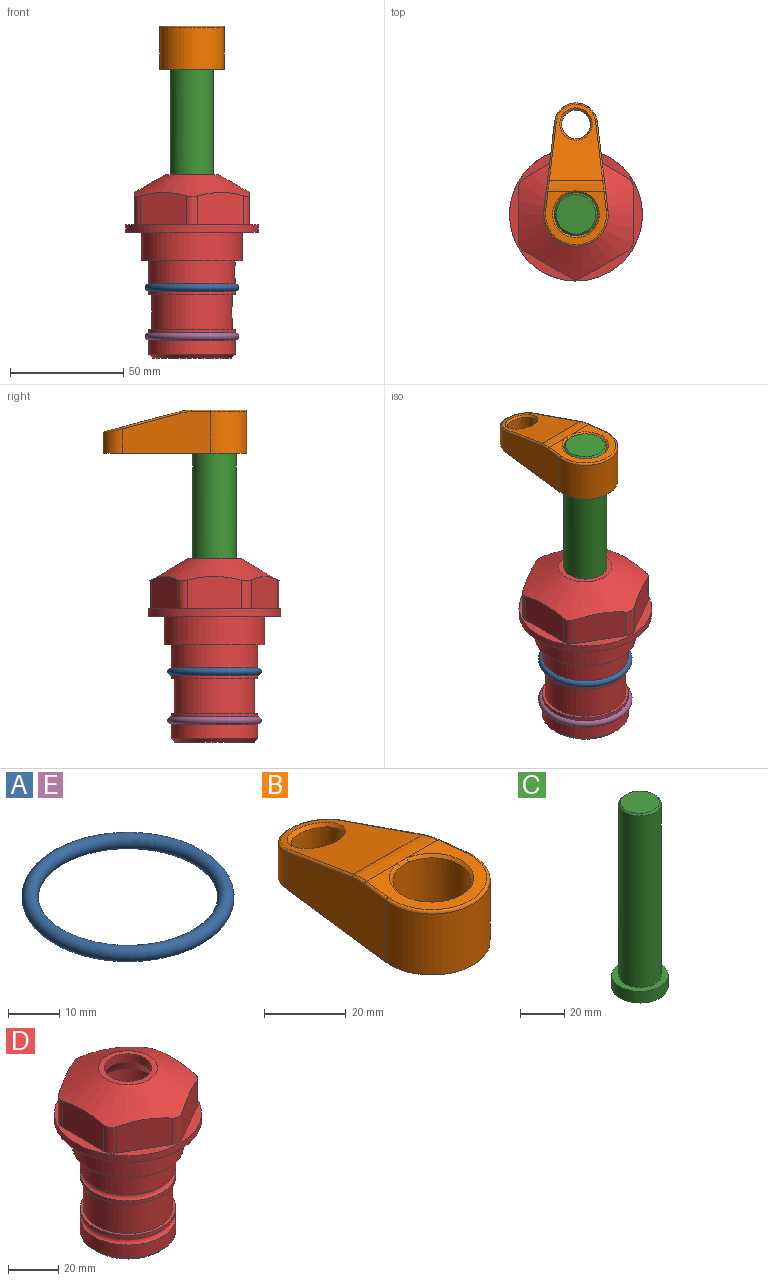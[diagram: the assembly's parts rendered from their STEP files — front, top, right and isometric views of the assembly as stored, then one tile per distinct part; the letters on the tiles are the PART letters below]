
ASSEMBLY  parts=5 mates=4
PART A: 1 faces, bbox 44.7x44.7x3.2 mm
  f0: torus R=19.05mm, axis (0,0,1), area 1193.9mm2
PART B: 31 faces, bbox 31.7x65.5x19.8 mm
  f0: plane 39.12x18.26mm, normal (0.99,0.12,0), area 612.2mm2, adj f1,f4,f7,f11,f13,f15
  f1: cylinder r=9.53mm len=18.91mm, axis (0,0,-1), area 296.1mm2, adj f0,f2,f7,f17
  f2: plane 39.12x18.26mm, normal (-0.99,0.12,0), area 612.2mm2, adj f1,f4,f7,f12,f14,f16
  f3: cylinder r=6.35mm len=12.7mm, axis (0,0,-1), area 362.4mm2, adj f7,f18
  f4: cylinder r=14.29mm len=28.58mm, axis (0,0,-1), area 882.2mm2, adj f0,f2,f7,f10
  f5: cylinder r=9.53mm len=19.05mm, axis (0,0,-1), area 1092.6mm2, adj f7,f19,f20
  f6: plane 26.99x23.69mm, normal (0,0,1), area 216.2mm2, adj f9,f10,f11,f12,f19
  f7: plane 63.5x28.58mm, normal (0,0,-1), area 661.8mm2, adj f0,f1,f2,f3,f4,f5,f22,f23
  f8: plane 33.52x23.6mm, normal (0,0.26,0.97), area 486mm2, adj f9,f15,f16,f17,f18
  f9: cylinder r=19.05mm len=24.72mm, axis (1,0,0), area 120.4mm2, adj f6,f8,f13,f14,f20
  f10: torus R=13.49mm, axis (0,0,1), area 59mm2, adj f4,f6,f11,f12
  f11: cylinder r=0.79mm len=8.67mm, axis (0.12,-0.99,0), area 10.8mm2, adj f0,f6,f10,f13
  f12: cylinder r=0.79mm len=8.67mm, axis (0.12,0.99,0), area 10.8mm2, adj f2,f6,f10,f14
  f13: bspline ~4.95x1.42mm, area 6.1mm2, adj f0,f9,f11,f15
  f14: bspline ~4.95x1.42mm, area 6.1mm2, adj f2,f9,f12,f16
  f15: cylinder r=0.79mm len=25.95mm, axis (0.12,-0.96,0.26), area 32.9mm2, adj f0,f8,f13,f17
  f16: cylinder r=0.79mm len=25.95mm, axis (0.12,0.96,-0.26), area 32.9mm2, adj f2,f8,f14,f17
  f17: bspline ~18.91x8.38mm, area 30mm2, adj f1,f8,f15,f16
  f18: bspline ~14.29x14.29mm, area 48.3mm2, adj f3,f8
  f19: cone r=9.53mm half-angle=45deg, axis (0,0,1), area 66.5mm2, adj f5,f6,f20
  f20: bspline ~3.22x0.96mm, area 3.5mm2, adj f5,f9,f19
  f21: plane 2.75x2.72mm, normal (0,0,-1), area 2.9mm2, adj f23,f25,f28
  f22: plane 23.05x15.88mm, normal (-0.99,-0.12,0), area 323.6mm2, adj f7,f25,f26,f27,f28,f29
  f23: plane 23.05x15.88mm, normal (0.99,-0.12,0), area 323.6mm2, adj f7,f21,f25,f27,f28,f30
  f24: cylinder r=9.53mm len=10.69mm, axis (0,0,-1), area 114.7mm2, adj f7,f27,f29,f30
  f25: cylinder r=12.7mm len=20.59mm, axis (0,0,-1), area 381.1mm2, adj f7,f21,f22,f23,f26,f28
  f26: plane 2.75x2.72mm, normal (0,0,-1), area 2.9mm2, adj f22,f25,f28
  f27: plane 19.72x18.37mm, normal (0,-0.26,-0.97), area 291.8mm2, adj f22,f23,f24,f28,f29,f30
  f28: cylinder r=15.88mm len=19.92mm, axis (1,0,0), area 54.8mm2, adj f21,f22,f23,f25,f26,f27
  f29: cylinder r=1.59mm len=11mm, axis (0,0,-1), area 34.7mm2, adj f7,f22,f24,f27
  f30: cylinder r=1.59mm len=11mm, axis (0,0,-1), area 34.7mm2, adj f7,f23,f24,f27
PART C: 6 faces, bbox 25.4x25.4x101.6 mm
  f0: plane 17.46x17.46mm, normal (0,0,1), area 239.5mm2, adj f5
  f1: plane 25.4x25.4mm, normal (0,0,-1), area 506.7mm2, adj f2
  f2: cylinder r=12.7mm len=25.4mm, axis (0,0,1), area 506.7mm2, adj f1,f3
  f3: plane 25.4x25.4mm, normal (0,0,1), area 221.7mm2, adj f2,f4
  f4: cylinder r=9.53mm len=94.46mm, axis (0,0,1), area 5653mm2, adj f3,f5
  f5: cone r=8.73mm half-angle=45deg, axis (0,0,-1), area 64.4mm2, adj f0,f4
PART D: 36 faces, bbox 58.7x58.7x81 mm
  f0: cylinder r=17.78mm len=35.56mm, axis (0,0,1), area 1670.8mm2, adj f23,f24,f31
  f1: cylinder r=19.05mm len=38.1mm, axis (0,0,1), area 1191.9mm2, adj f26,f27,f30
  f2: plane 58.66x58.66mm, normal (0,0,-1), area 1150.6mm2, adj f3,f28
  f3: cylinder r=29.33mm len=58.66mm, axis (0,0,-1), area 585.1mm2, adj f2,f4
  f4: plane 58.66x58.66mm, normal (0,0,1), area 475.9mm2, adj f3,f5,f6,f7,f8,f9,f10,f11
  f5: plane 20.32x14.34mm, normal (-0.5,0.87,0), area 324.4mm2, adj f4,f15,f16,f17
  f6: plane 20.32x14.34mm, normal (0.5,0.87,0), area 324.4mm2, adj f4,f14,f15,f17
  f7: plane 23.48x14.34mm, normal (1,0,0), area 324.4mm2, adj f4,f13,f14,f17
  f8: plane 20.32x14.34mm, normal (0.5,-0.87,0), area 324.4mm2, adj f4,f12,f13,f17
  f9: plane 20.32x14.34mm, normal (-0.5,-0.87,0), area 324.4mm2, adj f4,f11,f12,f17
  f10: plane 23.48x14.34mm, normal (-1,0,0), area 324.4mm2, adj f4,f11,f16,f17
  f11: cylinder r=5.08mm len=12.85mm, axis (0,0,-1), area 67.2mm2, adj f4,f9,f10,f17
  f12: cylinder r=5.08mm len=12.85mm, axis (0,0,-1), area 67.2mm2, adj f4,f8,f9,f17
  f13: cylinder r=5.08mm len=12.85mm, axis (0,0,-1), area 67.2mm2, adj f4,f7,f8,f17
  f14: cylinder r=5.08mm len=12.85mm, axis (0,0,-1), area 67.2mm2, adj f4,f6,f7,f17
  f15: cylinder r=5.08mm len=12.85mm, axis (0,0,-1), area 67.2mm2, adj f4,f5,f6,f17
  f16: cylinder r=5.08mm len=12.85mm, axis (0,0,-1), area 67.2mm2, adj f4,f5,f10,f17
  f17: cone r=11.73mm half-angle=60deg, axis (0,0,-1), area 2071.8mm2, adj f5,f6,f7,f8,f9,f10,f11,f12
  f18: plane 23.46x23.46mm, normal (0,0,1), area 147.4mm2, adj f17,f35
  f19: plane 34.93x34.93mm, normal (0,0,-1), area 958mm2, adj f29
  f20: cylinder r=19.05mm len=38.1mm, axis (0,0,1), area 760.1mm2, adj f21,f29
  f21: torus R=19.05mm, axis (0,0,1), area 565.3mm2, adj f20,f22
  f22: cylinder r=19.05mm len=38.1mm, axis (0,0,1), area 190mm2, adj f21,f23
  f23: plane 38.1x38.1mm, normal (0,0,1), area 146.9mm2, adj f0,f22
  f24: plane 38.1x38.1mm, normal (0,0,-1), area 146.9mm2, adj f0,f25
  f25: cylinder r=19.05mm len=38.1mm, axis (0,0,1), area 190mm2, adj f24,f26
  f26: torus R=19.05mm, axis (0,0,1), area 565.3mm2, adj f1,f25
  f27: plane 44.45x44.45mm, normal (0,0,-1), area 411.7mm2, adj f1,f28
  f28: cylinder r=22.23mm len=44.45mm, axis (0,0,1), area 1773.5mm2, adj f2,f27
  f29: cone r=19.05mm half-angle=45deg, axis (0,0,1), area 257.5mm2, adj f19,f20
  f30: cylinder r=3.17mm len=6.75mm, axis (-1,0,0), area 128mm2, adj f1,f33
  f31: cylinder r=3.17mm len=6.35mm, axis (-1,0,0), area 102.5mm2, adj f0,f33
  f32: plane 25.4x25.4mm, normal (0,0,1), area 506.7mm2, adj f33
  f33: cylinder r=12.7mm len=66.42mm, axis (0,0,-1), area 5236.2mm2, adj f30,f31,f32,f34
  f34: cone r=9.53mm half-angle=30deg, axis (0,0,-1), area 443.4mm2, adj f33,f35
  f35: cylinder r=9.53mm len=19.05mm, axis (0,0,-1), area 240.9mm2, adj f18,f34
PART E: same geometry as A
PLACE A at identity
PLACE B rot(axis=(0,0,1),0deg) t=(0,0,27.55)mm
PLACE C rot(axis=(0,0,1),0deg) t=(0,0,27.55)mm
PLACE D at identity fixed
PLACE E t=(0,0,-21.59)mm
MATE fastened E.f0 <-> D.f0  axis (0,0,1) through (0,0,-46.1)mm
MATE fastened C.f2 <-> B.f4  axis (0,0,1) through (0,0,91.05)mm
MATE fastened A.f0 <-> D.f0  axis (0,0,1) through (0,0,-24.51)mm
MATE cylindrical C.f2 <-> D.f0  axis (0,0,-1) through (0,0,-10.55)mm
